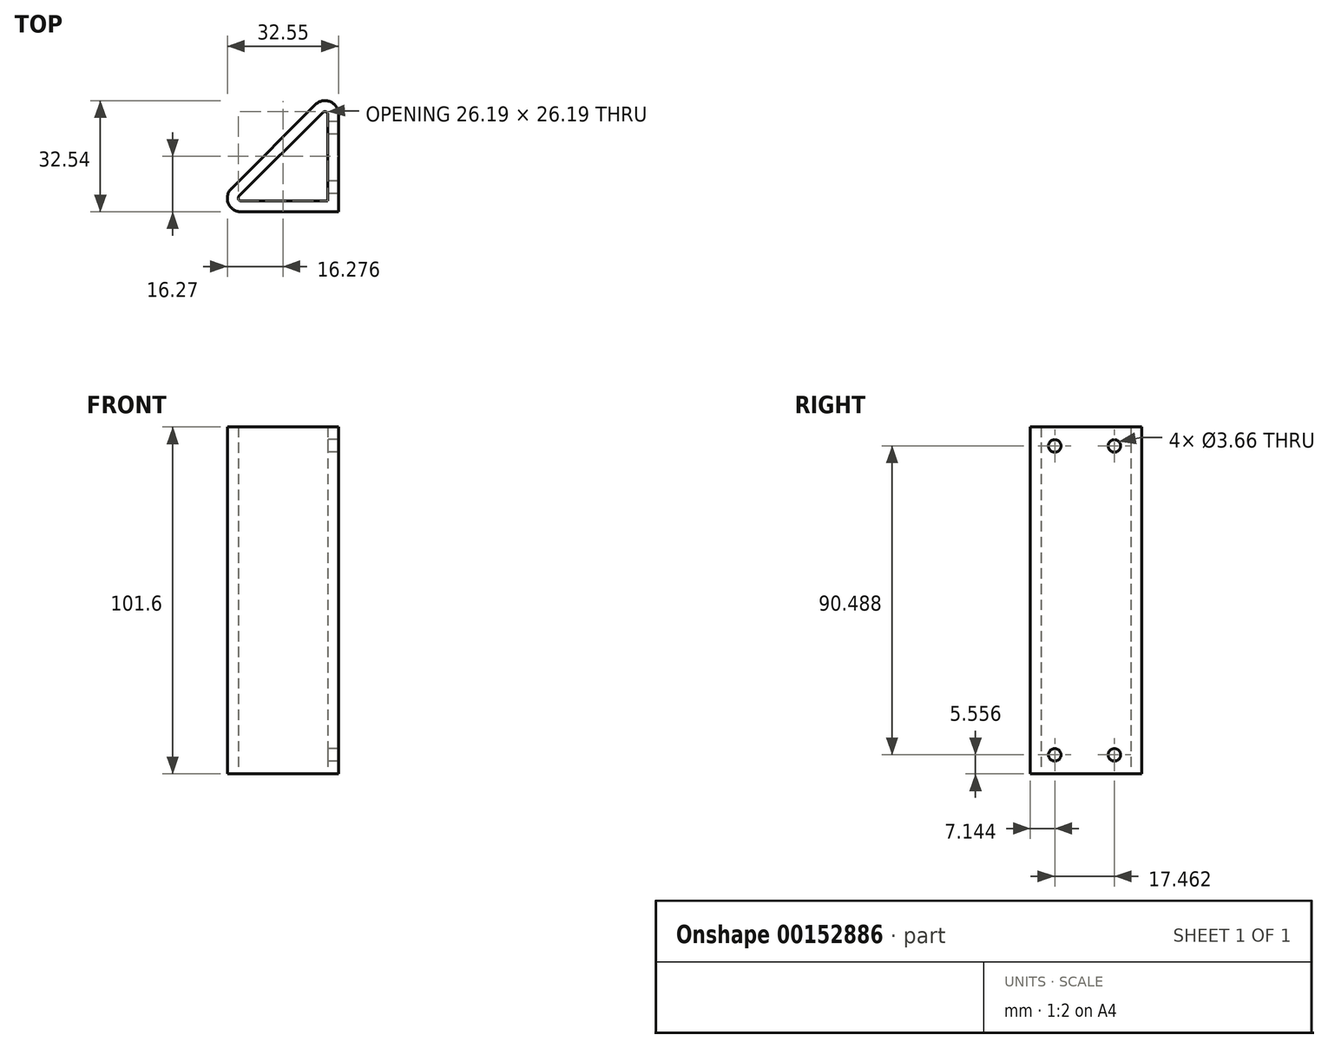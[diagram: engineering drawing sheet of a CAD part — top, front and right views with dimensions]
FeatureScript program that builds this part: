
annotation { "Feature Type Name" : "Feature", "Feature Type Description" : "" }
export const myFeature = defineFeature(function(context is Context, id is Id, definition is map)
    precondition{}
    {
        {
            var Q0;
            Q0=qCreatedBy(makeId("Top.planeOp"),FACE);
            var sketch = newSketch(context, id + "F0", { "sketchPlane" : qUnion([Q0])});
            skLineSegment(sketch, "E0", {"start": v(0.56, -1.36) * mm, "end": v(25.96, -1.36) * mm});
            skLineSegment(sketch, "E1", {"start": v(25.96, -1.36) * mm, "end": v(25.96, 24.04) * mm});
            skLineSegment(sketch, "E2", {"start": v(24.6, 24.6) * mm, "end": v(0, 0) * mm});
            skArc(sketch, "E3", {"start": v(25.96, 24.04) * mm, "mid": v(25.47, 24.78) * mm, "end": v(24.6, 24.6) * mm});
            skArc(sketch, "E4", {"start": v(29.14, 24.04) * mm, "mid": v(26.69, 27.71) * mm, "end": v(22.36, 26.85) * mm});
            skArc(sketch, "E5", {"start": v(-2.25, 2.25) * mm, "mid": v(-3.1, -2.08) * mm, "end": v(0.56, -4.53) * mm});
            skLineSegment(sketch, "E6", {"start": v(-2.25, 2.25) * mm, "end": v(22.36, 26.85) * mm});
            skLineSegment(sketch, "E7", {"start": v(0.56, -4.53) * mm, "end": v(29.14, -4.53) * mm});
            skLineSegment(sketch, "E8", {"start": v(29.14, -4.53) * mm, "end": v(29.14, 24.04) * mm});
            skLineSegment(sketch, "E9", {"start": v(25.96, -1.36) * mm, "end": v(25.96, -4.53) * mm, "construction": true});
            skLineSegment(sketch, "E10", {"start": v(25.96, -1.36) * mm, "end": v(29.14, -1.36) * mm, "construction": true});
            skArc(sketch, "E11", {"start": v(0, 0) * mm, "mid": v(-0.17, -0.87) * mm, "end": v(0.56, -1.36) * mm});
            skSolve(sketch);
        }
        {
            var Q0;
            Q0=qSketchRegion(id+"F0",true);
            extrude(context, id + "F1", {"entities" : qUnion([Q0]), "depth" : 101.6 * mm});
        }
        {
            var Q0;
            Q0=makeQuery(id+"F1.opExtrude","SWEPT_FACE",FACE,{"disambiguationData":[OSD([sQuery(id+"F0.wireOp",EDGE,"E1")])]});
            var sketch = newSketch(context, id + "F2", { "sketchPlane" : qUnion([Q0])});
            skLineSegment(sketch, "E12", {"start": v(-24.04, 50.8) * mm, "end": v(1.36, 50.8) * mm, "construction": true});
            skLineSegment(sketch, "E13.bottom", {"start": v(-24.04, 0) * mm, "end": v(-20.08, 0) * mm, "construction": true});
            skLineSegment(sketch, "E13.top", {"start": v(-24.04, 5.56) * mm, "end": v(-20.08, 5.56) * mm, "construction": true});
            skLineSegment(sketch, "E13.left", {"start": v(-24.04, 0) * mm, "end": v(-24.04, 5.56) * mm, "construction": true});
            skLineSegment(sketch, "E13.right", {"start": v(-20.08, 0) * mm, "end": v(-20.08, 5.56) * mm, "construction": true});
            skLineSegment(sketch, "E14.bottom", {"start": v(-20.08, 5.56) * mm, "end": v(-2.61, 5.56) * mm, "construction": true});
            skLineSegment(sketch, "E14.top", {"start": v(-20.08, 96.04) * mm, "end": v(-2.61, 96.04) * mm, "construction": true});
            skLineSegment(sketch, "E14.left", {"start": v(-20.08, 5.56) * mm, "end": v(-20.08, 96.04) * mm, "construction": true});
            skLineSegment(sketch, "E14.right", {"start": v(-2.61, 5.56) * mm, "end": v(-2.61, 96.04) * mm, "construction": true});
            skPoint(sketch, "E14.middle", {"position": v(-11.34, 50.8) * mm});
            skCircle(sketch, "E15", {"center": v(-20.08, 5.56) * mm, "radius": 1.83 * mm});
            skCircle(sketch, "E16", {"center": v(-2.61, 5.56) * mm, "radius": 1.83 * mm});
            skCircle(sketch, "E17", {"center": v(-2.61, 96.04) * mm, "radius": 1.83 * mm});
            skCircle(sketch, "E18", {"center": v(-20.08, 96.04) * mm, "radius": 1.83 * mm});
            skSolve(sketch);
        }
        {
            var Q0;
            Q0=qSketchRegion(id+"F2",true);
            var Q1;
            Q1=makeQuery(id+"F1.opExtrude","SWEPT_FACE",FACE,{"disambiguationData":[OSD([sQuery(id+"F0.wireOp",EDGE,"E8")])]});
            extrude(context, id + "F3", {"entities" : qUnion([Q0]), "operationType" : NewBodyOperationType.REMOVE, "endBound" : BoundingType.UP_TO_SURFACE, "oppositeDirection" : true, "endBoundEntityFace" : qUnion([Q1]), "depth" : 25.4 * mm});
        }
    });
